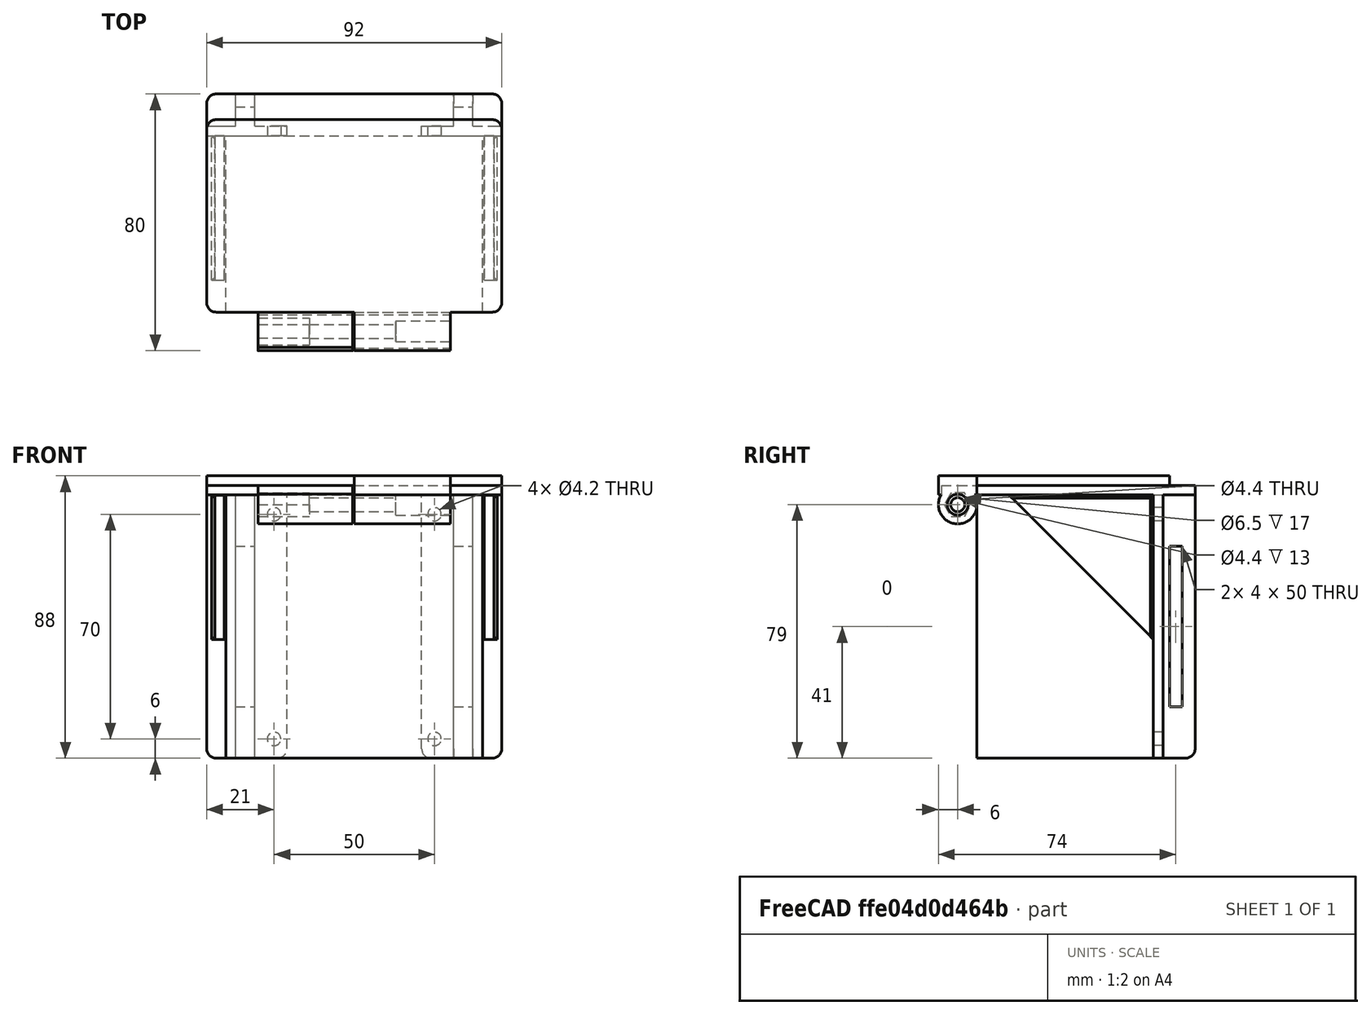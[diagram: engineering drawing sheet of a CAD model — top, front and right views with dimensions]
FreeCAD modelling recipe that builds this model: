
FCSTD DOCUMENT  (FreeCAD 0.15R4671 (Git))
Label: Enclosure_supports_with_Hood04
License: All rights reserved
LicenseURL: http://en.wikipedia.org/wiki/All_rights_reserved
objects: Drawing::FeatureViewPython×22, Part::Box×19, Part::Cut×10, Part::Cylinder×9, Part::MultiFuse×8, Part::Chamfer×8, Drawing::FeatureViewPart×2, Part::Fillet×2, Part::Prism×1, Drawing::FeaturePage×1
note: 57 computed .brp shape members not serialized (recipe doc carries the construction recipe); baked Part::Feature solids carry a one-line shape summary decoded from their .brp

FEATURE [Part::Box] Box  label="Cube"
  Height = 3
  Length = 92
  Placement = pos=(-6,0,0) rot=(0,0,1;0rad)
  Width = 68
FEATURE [Part::Cylinder] Cylinder
  Angle = 360
  Height = 29.5
  Placement = pos=(10,-6,-3) rot=(0,1,0;1.5708rad)
  Radius = 6
FEATURE [Part::Cylinder] Cylinder001
  Angle = 360
  Height = 30
  Placement = pos=(40,-6,-3) rot=(0,1,0;1.5708rad)
  Radius = 6
FEATURE [Part::Box] Box001  label="Cube001"
  Height = 3
  Length = 29.5
  Placement = pos=(10,-11,0) rot=(0,0,1;0rad)
  Width = 11
FEATURE [Part::Cylinder] Cylinder002
  Angle = 360
  Height = 30
  Placement = pos=(40,-6,-3) rot=(0,1,0;1.5708rad)
  Radius = 2.2
FEATURE [Part::Cylinder] Cylinder003
  Angle = 360
  Height = 30
  Placement = pos=(10,-6,-3) rot=(0,1,0;1.5708rad)
  Radius = 2.2
FEATURE [Part::Box] Box002  label="Cube002"
  Height = 3
  Length = 92
  Placement = pos=(-6,0,3) rot=(0,0,1;0rad)
  Width = 60
FEATURE [Part::Box] Box003  label="Cube003"
  Height = 6
  Length = 30
  Placement = pos=(40,-12,0) rot=(0,0,1;0rad)
  Width = 12
FEATURE [Part::Prism] Prism001
  Circumradius = 4.2
  Height = 16
  Placement = pos=(10,-6,-3) rot=(0.57735,0.57735,0.57735;2.0944rad)
  Polygon = 6
FEATURE [Part::Cylinder] Cylinder004
  Angle = 360
  Height = 17.5
  Placement = pos=(53,-6,-3) rot=(0,1,0;1.5708rad)
  Radius = 3.25
FEATURE [Part::Box] Box004  label="Cube004"
  Height = 45
  Length = 3
  Placement = pos=(80.5,10,-45) rot=(0,0,1;0rad)
  Width = 45
FEATURE [Part::Box] Box005  label="Cube005"
  Height = 45
  Length = 3
  Placement = pos=(-3.5,10,-45) rot=(0,0,1;0rad)
  Width = 45
FEATURE [Part::Box] Box006  label="Cube006"
  Height = 63.63
  Length = 3
  Placement = pos=(80.5,10,-90) rot=(1,0,0;0.785398rad)
  Width = 63.63
FEATURE [Part::Cut] Cut002
  Base = -> Box004
  Tool = -> Box006
FEATURE [Part::Box] Box007  label="Cube007"
  Height = 63.63
  Length = 3
  Placement = pos=(-3.5,10,-90) rot=(1,0,0;0.785398rad)
  Width = 63.63
FEATURE [Part::Cut] Cut003
  Base = -> Box005
  Tool = -> Box007
FEATURE [Part::Box] Box008  label="Cube008"
  Height = 82
  Length = 25
  Placement = pos=(-6,55,-82) rot=(0,0,1;0rad)
  Width = 3
FEATURE [Part::Box] Box009  label="Cube009"
  Height = 82
  Length = 25
  Placement = pos=(61,55,-82) rot=(0,0,1;0rad)
  Width = 3
FEATURE [Part::Cylinder] Cylinder005
  Angle = 360
  Height = 3
  Placement = pos=(15,58,-6) rot=(1,0,0;1.5708rad)
  Radius = 2.1
FEATURE [Part::Cylinder] Cylinder006
  Angle = 360
  Height = 3
  Placement = pos=(15,58,-76) rot=(1,0,0;1.5708rad)
  Radius = 2.1
FEATURE [Part::Cylinder] Cylinder007
  Angle = 360
  Height = 3
  Placement = pos=(65,58,-6) rot=(1,0,0;1.5708rad)
  Radius = 2.1
FEATURE [Part::Cylinder] Cylinder008
  Angle = 360
  Height = 3
  Placement = pos=(65,58,-76) rot=(1,0,0;1.5708rad)
  Radius = 2.1
FEATURE [Part::Box] Box011  label="Cube011"
  Height = 82
  Length = 6
  Placement = pos=(3,58,-82) rot=(0,0,1;0rad)
  Width = 10
FEATURE [Part::Box] Box012  label="Cube012"
  Height = 82
  Length = 6
  Placement = pos=(71,58,-82) rot=(0,0,1;0rad)
  Width = 10
FEATURE [Part::Box] Box013  label="Cube013"
  Height = 50
  Length = 6
  Placement = pos=(3,60,-66) rot=(0,0,1;0rad)
  Width = 4
FEATURE [Part::Box] Box014  label="Cube014"
  Height = 50
  Length = 6
  Placement = pos=(71,60,-66) rot=(0,0,1;0rad)
  Width = 4
FEATURE [Part::Box] Box015  label="G366"
  Height = 82
  Length = 80
  Placement = pos=(0,0,-82) rot=(0,0,1;0rad)
  Width = 55
FEATURE [Part::Cut] Cut
  Base = -> Cylinder
  Tool = -> Cylinder003
FEATURE [Part::Cut] Cut004
  Base = -> Cylinder001
  Tool = -> Cylinder002
FEATURE [Part::MultiFuse] Fusion
  Shapes = -> [Box,Box001,Cut]
FEATURE [Part::MultiFuse] Fusion001
  Shapes = -> [Cut004,Box003,Box002]
FEATURE [Part::Cut] Cut005
  Base = -> Fusion
  Tool = -> Prism001
FEATURE [Part::Cut] Cut006
  Base = -> Fusion001
  Tool = -> Cylinder004
FEATURE [Part::MultiFuse] Fusion002
  Shapes = -> [Cylinder005,Cylinder006]
FEATURE [Part::MultiFuse] Fusion003
  Shapes = -> [Cylinder007,Cylinder008]
FEATURE [Part::Cut] Cut007
  Base = -> Box008
  Tool = -> Fusion002
FEATURE [Part::Cut] Cut008
  Base = -> Box009
  Tool = -> Fusion003
FEATURE [Part::Cut] Cut009
  Base = -> Box011
  Tool = -> Box013
FEATURE [Part::Cut] Cut010
  Base = -> Box012
  Tool = -> Box014
FEATURE [Part::MultiFuse] Fusion004
  Shapes = -> [Cut007,Cut009]
FEATURE [Part::MultiFuse] Fusion005
  Shapes = -> [Cut008,Cut010]
FEATURE [Part::MultiFuse] Fusion006
  Shapes = -> [Cut002,Cut003,Cut005,Fusion004,Fusion005]
FEATURE [Drawing::FeatureViewPart] Ortho001  label="Ortho_-1_0"
  Direction = (0,1,0)
  HiddenWidth = 0.15
  LineWidth = 0.35
  Rotation = -90
  ShowHiddenLines = false
  ShowSmoothLines = false
  Source = -> Fusion006
  Tolerance = 0.05
  ViewResult = <g id="Ortho_-1_0"\n   transform="rotate(-90,125.25,42) translate(125.25,42) scale(1,1)"\n  >\n<g   stroke="rgb(0, 0, 0)"\n   stroke-width="0.35"\n   stroke-linecap="butt"\n   stroke-linejoin="miter"\n   fill="none"\n   transform="scale(1,-1)"\n  >\n<path id= "1" d=" M 0 9 L 0 71 " />\n<path id= "2" d=" M 0 -6 L 3 -6 " />\n<path id= "3" d=" M -82 19 L 0 19 " />\n<path id= "4" d=" M -82 9 L -82 19 " />\n<circle cx ="-76" cy ="15" r ="2.1" /><circle cx ="-6" cy ="15" r ="2.1" /><path id= "7" d=" M -82 9 L 0 9 " />\n<path id= "8" d=" M 0 -6 L 0 3 " />\n<path id= "9" d=" M 0 3 L 0 9 " />\n<path id= "10" d=" M 3 -6 L 3 86 " />\n<path id= "11" d=" M 0 86 L 3 86 " />\n<path id= "12" d=" M 0 71 L 0 77 " />\n<path id= "13" d=" M 0 77 L 0 86 " />\n<path id= "14" d=" M -82 71 L 0 71 " />\n<path id= "15" d=" M -82 61 L -82 71 " />\n<path id= "16" d=" M -82 61 L 0 61 " />\n<circle cx ="-6" cy ="65" r ="2.1" /><circle cx ="-76" cy ="65" r ="2.1" /><path id= "19" d=" M -82 86 L 0 86 " />\n<path id= "20" d=" M -82 77 L -82 86 " />\n<path id= "21" d=" M -82 -6 L 0 -6 " />\n<path id= "22" d=" M -82 -6 L -82 3 " />\n<path id= "23" d=" M -82 3 L -82 9 " />\n<path id= "24" d=" M -82 3 L 0 3 " />\n<path id= "25" d=" M -82 71 L -82 77 " />\n<path id= "26" d=" M -82 77 L 0 77 " />\n<path d="M-9,39.5 L-8.93298,39.5  L-8.73344,39.5  L-8.40581,39.5  L-7.95743,39.5  L-7.39831,39.5  L-6.74094,39.5  L-6,39.5  L-5.19205,39.5  L-4.33513,39.5  L-3.44838,39.5  L-2.55162,39.5  L-1.66487,39.5  L-0.807954,39.5  L8.21565e-14,39.5 " /><path id= "28" d=" M -9 19 L -9 39.5 " />\n</g>\n</g>
  Visible = true
  X = 125.25
  Y = 42
FEATURE [Drawing::FeatureViewPart] Ortho002  label="Ortho_1_0"
  Direction = (0,-1,0)
  HiddenWidth = 0.15
  LineWidth = 0.35
  Rotation = 90
  ShowHiddenLines = false
  ShowSmoothLines = false
  Source = -> Fusion006
  Tolerance = 0.05
  ViewResult = <blob: 2087 chars omitted>
  Visible = true
  X = 174.75
  Y = 42
FEATURE [Drawing::FeatureViewPython] dim001  # drawing view (typed FeaturePython)
  Rotation = 0
  ViewResult = <g> \n  <line x1="166.750000" y1="124.000000" x2="154.257392" y2="124.000000" style="stroke:rgb(0,0,255);stroke-width:0.50" />\n<line x1="166.750000" y1="42.000000" x2="154.257392" y2="42.000000" style="stroke:rgb(0,0,255);stroke-width:0.50" />\n<line x1="155.257392" y1="124.000000" x2="155.257392" y2="42.000000" style="stroke:rgb(0,0,255);stroke-width:0.50" /> \n  <polygon points="155.257392,42.000000 154.257392,45.000000 155.257392,46.000000 156.257392,45.000000" style="fill:rgb(0,0,255);stroke:rgb(0,0,255);stroke-width:0" /><polygon points="155.257392,124.000000 156.257392,121.000000 155.257392,120.000000 154.257392,121.000000" style="fill:rgb(0,0,255);stroke:rgb(0,0,255);stroke-width:0" /> \n  <text x="153.257392" y="83.000000" font-family="inherit" font-size="3.6" fill="rgb(0,0,255)" text-anchor="middle" transform="rotate(-90.000000 153.257392,83.000000)" >82</text> </g>
  Visible = true
  X = 0
  Y = 0
  arrowL1 = 3
  arrowL2 = 1
  arrowW = 2
  arrow_scheme = 0
  autoPlaceOffset = 2
  autoPlaceText = true
  click1_x = 155.257
  click1_y = 108.709
  click2_x = 155.257
  click2_y = 108.709
  comma_decimal_place = false
  dimension_line_overshoot = 1
  gap_datum_points = 2
  halfDimension_linear = false
  lineColor = rgb(0,0,255)
  strokeWidth = 0.5
  textFormat_linear = %(value)3.3f
  textRenderer_color = rgb(0,0,255)
  textRenderer_family = inherit
  textRenderer_size = 3.6
  unit_custom_scale = 1
  unit_scheme = 0
FEATURE [Drawing::FeatureViewPython] dim002  # drawing view (typed FeaturePython)
  Rotation = 0
  ViewResult = <g> \n  <line x1="214.250000" y1="40.000000" x2="214.250000" y2="33.983509" style="stroke:rgb(0,0,255);stroke-width:0.50" />\n<line x1="260.750000" y1="40.000000" x2="260.750000" y2="33.983509" style="stroke:rgb(0,0,255);stroke-width:0.50" />\n<line x1="214.250000" y1="34.983509" x2="260.750000" y2="34.983509" style="stroke:rgb(0,0,255);stroke-width:0.50" /> \n  <polygon points="260.750000,34.983509 257.750000,33.983509 256.750000,34.983509 257.750000,35.983509" style="fill:rgb(0,0,255);stroke:rgb(0,0,255);stroke-width:0" /><polygon points="214.250000,34.983509 217.250000,35.983509 218.250000,34.983509 217.250000,33.983509" style="fill:rgb(0,0,255);stroke:rgb(0,0,255);stroke-width:0" /> \n  <text x="237.500000" y="32.983509" font-family="inherit" font-size="3.6" fill="rgb(0,0,255)" text-anchor="middle" transform="rotate(0.000000 237.500000,32.983509)" >46.5</text> </g>
  Visible = true
  X = 0
  Y = 0
  arrowL1 = 3
  arrowL2 = 1
  arrowW = 2
  arrow_scheme = 0
  autoPlaceOffset = 2
  autoPlaceText = true
  click1_x = 220.02
  click1_y = 34.9835
  click2_x = 220.02
  click2_y = 34.9835
  comma_decimal_place = false
  dimension_line_overshoot = 1
  gap_datum_points = 2
  halfDimension_linear = false
  lineColor = rgb(0,0,255)
  strokeWidth = 0.5
  textFormat_linear = %(value)3.3f
  textRenderer_color = rgb(0,0,255)
  textRenderer_family = inherit
  textRenderer_size = 3.6
  unit_custom_scale = 1
  unit_scheme = 0
FEATURE [Drawing::FeatureViewPython] centerLines001  # drawing view (typed FeaturePython)
  Rotation = 0
  ViewResult = <g transform="scale(1.000000,1.000000)" stroke="rgb(0,0,255)"  stroke-width="0.320000" > <path d="M 189.750000,118.000000 L 189.750000,121.000000 M 189.750000,123.000000 L 189.750000,124.803428 "/>\n<path d="M 189.750000,118.000000 L 192.750000,118.000000 M 194.750000,118.000000 L 197.083406,118.000000 "/>\n<path d="M 189.750000,118.000000 L 189.750000,115.000000 M 189.750000,113.000000 L 189.750000,108.179034 "/>\n<path d="M 189.750000,118.000000 L 186.750000,118.000000 M 184.750000,118.000000 L 182.145544,118.000000 "/> </g> 
  Visible = true
  X = 0
  Y = 0
  centerLine_color = rgb(0,0,255)
  centerLine_len_dash = 6
  centerLine_len_dot = 3
  centerLine_len_gap = 2
  centerLine_width = 0.32
  click1_x = 197.083
  click1_y = 124.803
  click2_x = 182.146
  click2_y = 108.179
FEATURE [Drawing::FeatureViewPython] centerLines002  # drawing view (typed FeaturePython)
  Rotation = 0
  ViewResult = <g transform="scale(1.000000,1.000000)" stroke="rgb(0,0,255)"  stroke-width="0.320000" > <path d="M 189.750000,118.000000 L 189.750000,121.000000 M 189.750000,123.000000 L 189.750000,126.008095 "/>\n<path d="M 189.750000,118.000000 L 192.750000,118.000000 M 194.750000,118.000000 L 200.750000,118.000000 M 202.750000,118.000000 L 205.750000,118.000000 M 207.750000,118.000000 L 213.750000,118.000000 M 215.750000,118.000000 L 218.750000,118.000000 M 220.750000,118.000000 L 226.750000,118.000000 M 228.750000,118.000000 L 231.750000,118.000000 M 233.750000,118.000000 L 239.750000,118.000000 M 241.750000,118.000000 L 244.750000,118.000000 M 246.750000,118.000000 L 249.847790,118.000000 "/>\n<path d="M 189.750000,118.000000 L 189.750000,115.000000 M 189.750000,113.000000 L 189.750000,107.697167 "/>\n<path d="M 189.750000,118.000000 L 192.750000,118.000000 M 194.750000,118.000000 L 200.750000,118.000000 M 202.750000,118.000000 L 205.750000,118.000000 M 207.750000,118.000000 L 213.750000,118.000000 M 215.750000,118.000000 L 218.750000,118.000000 M 220.750000,118.000000 L 223.826998,118.000000 "/> </g> 
  Visible = true
  X = 0
  Y = 0
  centerLine_color = rgb(0,0,255)
  centerLine_len_dash = 6
  centerLine_len_dot = 3
  centerLine_len_gap = 2
  centerLine_width = 0.32
  click1_x = 249.848
  click1_y = 126.008
  click2_x = 223.827
  click2_y = 107.697
FEATURE [Drawing::FeatureViewPython] centerLines003  # drawing view (typed FeaturePython)
  Rotation = 0
  ViewResult = <g transform="scale(1.000000,1.000000)" stroke="rgb(0,0,255)"  stroke-width="0.320000" > <path d="M 189.750000,118.000000 L 189.750000,115.000000 M 189.750000,113.000000 L 189.750000,107.000000 M 189.750000,105.000000 L 189.750000,102.000000 M 189.750000,100.000000 L 189.750000,94.000000 M 189.750000,92.000000 L 189.750000,89.000000 M 189.750000,87.000000 L 189.750000,81.000000 M 189.750000,79.000000 L 189.750000,76.000000 M 189.750000,74.000000 L 189.750000,68.000000 M 189.750000,66.000000 L 189.750000,63.000000 M 189.750000,61.000000 L 189.750000,56.378383 "/>\n<path d="M 189.750000,118.000000 L 192.750000,118.000000 M 194.750000,118.000000 L 200.750000,118.000000 M 202.750000,118.000000 L 205.750000,118.000000 M 207.750000,118.000000 L 213.750000,118.000000 M 215.750000,118.000000 L 218.750000,118.000000 M 220.750000,118.000000 L 226.750000,118.000000 M 228.750000,118.000000 L 231.750000,118.000000 M 233.750000,118.000000 L 239.750000,118.000000 M 241.750000,118.000000 L 244.750000,118.000000 "/>\n<path d="M 189.750000,118.000000 L 189.750000,115.000000 M 189.750000,113.000000 L 189.750000,107.000000 M 189.750000,105.000000 L 189.750000,102.000000 M 189.750000,100.000000 L 189.750000,94.000000 M 189.750000,92.000000 L 189.750000,89.000000 M 189.750000,87.000000 L 189.750000,81.000000 M 189.750000,79.000000 L 189.750000,76.000000 M 189.750000,74.000000 L 189.750000,68.000000 M 189.750000,66.000000 L 189.750000,63.000000 M 189.750000,61.000000 L 189.750000,55.000000 M 189.750000,53.000000 L 189.750000,50.000000 M 189.750000,48.000000 L 189.750000,42.163320 "/>\n<path d="M 189.750000,118.000000 L 192.750000,118.000000 M 194.750000,118.000000 L 200.750000,118.000000 M 202.750000,118.000000 L 205.750000,118.000000 M 207.750000,118.000000 L 213.750000,118.000000 M 215.750000,118.000000 L 218.750000,118.000000 M 220.750000,118.000000 L 226.750000,118.000000 "/> </g> 
  Visible = true
  X = 0
  Y = 0
  centerLine_color = rgb(0,0,255)
  centerLine_len_dash = 6
  centerLine_len_dot = 3
  centerLine_len_gap = 2
  centerLine_width = 0.32
  click1_x = 246.475
  click1_y = 56.3784
  click2_x = 227.923
  click2_y = 42.1633
FEATURE [Drawing::FeatureViewPython] dim003  # drawing view (typed FeaturePython)
  Rotation = 0
  ViewResult = <g> \n  <line x1="189.750000" y1="116.000000" x2="189.750000" y2="111.770659" style="stroke:rgb(0,0,255);stroke-width:0.50" />\n<line x1="197.083406" y1="116.000000" x2="197.083406" y2="111.770659" style="stroke:rgb(0,0,255);stroke-width:0.50" />\n<line x1="189.750000" y1="112.770659" x2="197.083406" y2="112.770659" style="stroke:rgb(0,0,255);stroke-width:0.50" /> \n  <polygon points="197.083406,112.770659 200.083406,113.770659 201.083406,112.770659 200.083406,111.770659" style="fill:rgb(0,0,255);stroke:rgb(0,0,255);stroke-width:0" /><polygon points="189.750000,112.770659 186.750000,111.770659 185.750000,112.770659 186.750000,113.770659" style="fill:rgb(0,0,255);stroke:rgb(0,0,255);stroke-width:0" /> \n  <text x="193.416703" y="110.770659" font-family="inherit" font-size="3.6" fill="rgb(0,0,255)" text-anchor="middle" transform="rotate(0.000000 193.416703,110.770659)" >7.333</text> </g>
  Visible = true
  X = 0
  Y = 0
  arrowL1 = 3
  arrowL2 = 1
  arrowW = 2
  arrow_scheme = 0
  autoPlaceOffset = 2
  autoPlaceText = true
  click1_x = 200.722
  click1_y = 112.771
  click2_x = 200.722
  click2_y = 112.771
  comma_decimal_place = false
  dimension_line_overshoot = 1
  gap_datum_points = 2
  halfDimension_linear = false
  lineColor = rgb(0,0,255)
  strokeWidth = 0.5
  textFormat_linear = %(value)3.3f
  textRenderer_color = rgb(0,0,255)
  textRenderer_family = inherit
  textRenderer_size = 3.6
  unit_custom_scale = 1
  unit_scheme = 0
FEATURE [Drawing::FeatureViewPython] centerLines004  # drawing view (typed FeaturePython)
  Rotation = 0
  ViewResult = <g transform="scale(1.000000,1.000000)" stroke="rgb(0,0,255)"  stroke-width="0.320000" > <path d="M 110.250000,48.000000 L 110.250000,51.000000 M 110.250000,53.000000 L 110.250000,59.000000 "/>\n<path d="M 110.250000,48.000000 L 110.250000,45.000000 M 110.250000,43.000000 L 110.250000,37.000000 M 110.250000,35.000000 L 110.250000,34.274134 "/> </g> 
  Visible = true
  X = 0
  Y = 0
  centerLine_color = rgb(0,0,255)
  centerLine_len_dash = 6
  centerLine_len_dot = 3
  centerLine_len_gap = 2
  centerLine_width = 0.32
  click1_x = 114.186
  click1_y = 60.4838
  click2_x = 114.003
  click2_y = 34.2741
FEATURE [Drawing::FeatureViewPython] dimStack001  # drawing view (typed FeaturePython)
  Rotation = 0
  ViewResult = <g> <line x1="189.750000" y1="106.179033" x2="189.750000" y2="80.378158" style="stroke:rgb(0,0,255);stroke-width:0.50" />\n<line x1="226.750000" y1="115.999999" x2="226.750000" y2="80.378158" style="stroke:rgb(0,0,255);stroke-width:0.50" />\n<line x1="189.750000" y1="81.378158" x2="226.750000" y2="81.378158" style="stroke:rgb(0,0,255);stroke-width:0.50" />\n<polygon points="189.750000,81.378158 192.750000,82.378158 193.750000,81.378158 192.750000,80.378158" style="fill:rgb(0,0,255);stroke:rgb(0,0,255);stroke-width:0" />\n<polygon points="226.750000,81.378158 223.750000,80.378158 222.750000,81.378158 223.750000,82.378158" style="fill:rgb(0,0,255);stroke:rgb(0,0,255);stroke-width:0" />\n<text x="208.250000" y="79.378158" font-family="inherit" font-size="3.6" fill="rgb(0,0,255)" text-anchor="middle" transform="rotate(0.000000 208.250000,79.378158)" >37</text> </g> 
  Visible = true
  X = 0
  Y = 0
  arrowL1 = 3
  arrowL2 = 1
  arrowW = 2
  arrow_scheme = 0
  autoPlaceOffset = 2
  click1_x = 210.777
  click1_y = 81.3782
  comma_decimal_place = false
  dimension_line_overshoot = 1
  gap_datum_points = 2
  lineColor = rgb(0,0,255)
  stack_offset = 7
  stack_offset0 = 0
  strokeWidth = 0.5
  textFormat_linear = %(value)3.3f
  textRenderer_color = rgb(0,0,255)
  textRenderer_family = inherit
  textRenderer_size = 3.6
  unit_custom_scale = 1
  unit_scheme = 0
FEATURE [Drawing::FeatureViewPython] dimStack002  # drawing view (typed FeaturePython)
  Rotation = 0
  ViewResult = <g> <line x1="168.750000" y1="126.000000" x2="168.750000" y2="129.298898" style="stroke:rgb(0,0,255);stroke-width:0.50" />\n<line x1="260.750000" y1="126.000000" x2="260.750000" y2="129.298898" style="stroke:rgb(0,0,255);stroke-width:0.50" />\n<line x1="168.750000" y1="128.298898" x2="260.750000" y2="128.298898" style="stroke:rgb(0,0,255);stroke-width:0.50" />\n<polygon points="168.750000,128.298898 171.750000,129.298898 172.750000,128.298898 171.750000,127.298898" style="fill:rgb(0,0,255);stroke:rgb(0,0,255);stroke-width:0" />\n<polygon points="260.750000,128.298898 257.750000,127.298898 256.750000,128.298898 257.750000,129.298898" style="fill:rgb(0,0,255);stroke:rgb(0,0,255);stroke-width:0" />\n<text x="214.750000" y="126.298898" font-family="inherit" font-size="3.6" fill="rgb(0,0,255)" text-anchor="middle" transform="rotate(0.000000 214.750000,126.298898)" >92</text> </g> 
  Visible = true
  X = 0
  Y = 0
  arrowL1 = 3
  arrowL2 = 1
  arrowW = 2
  arrow_scheme = 0
  autoPlaceOffset = 2
  click1_x = 214.076
  click1_y = 128.299
  comma_decimal_place = false
  dimension_line_overshoot = 1
  gap_datum_points = 2
  lineColor = rgb(0,0,255)
  stack_offset = 7
  stack_offset0 = 0
  strokeWidth = 0.5
  textFormat_linear = %(value)3.3f
  textRenderer_color = rgb(0,0,255)
  textRenderer_family = inherit
  textRenderer_size = 3.6
  unit_custom_scale = 1
  unit_scheme = 0
FEATURE [Drawing::FeatureViewPython] dimStack003  # drawing view (typed FeaturePython)
  Rotation = 0
  ViewResult = <g> <line x1="193.750000" y1="98.240299" x2="235.750000" y2="98.240299" style="stroke:rgb(0,0,255);stroke-width:0.50" />\n<polygon points="193.750000,98.240299 196.750000,99.240299 197.750000,98.240299 196.750000,97.240299" style="fill:rgb(0,0,255);stroke:rgb(0,0,255);stroke-width:0" />\n<polygon points="235.750000,98.240299 232.750000,97.240299 231.750000,98.240299 232.750000,99.240299" style="fill:rgb(0,0,255);stroke:rgb(0,0,255);stroke-width:0" />\n<text x="214.750000" y="96.240299" font-family="inherit" font-size="3.6" fill="rgb(0,0,255)" text-anchor="middle" transform="rotate(0.000000 214.750000,96.240299)" >42</text> </g> 
  Visible = true
  X = 0
  Y = 0
  arrowL1 = 3
  arrowL2 = 1
  arrowW = 2
  arrow_scheme = 0
  autoPlaceOffset = 2
  click1_x = 217.008
  click1_y = 98.2403
  comma_decimal_place = false
  dimension_line_overshoot = 1
  gap_datum_points = 2
  lineColor = rgb(0,0,255)
  stack_offset = 7
  stack_offset0 = 0
  strokeWidth = 0.5
  textFormat_linear = %(value)3.3f
  textRenderer_color = rgb(0,0,255)
  textRenderer_family = inherit
  textRenderer_size = 3.6
  unit_custom_scale = 1
  unit_scheme = 0
FEATURE [Drawing::FeatureViewPython] centerLines005  # drawing view (typed FeaturePython)
  Rotation = 0
  ViewResult = <g transform="scale(1.000000,1.000000)" stroke="rgb(0,0,255)"  stroke-width="0.320000" > <path d="M 60.250000,118.000000 L 60.250000,115.000000 M 60.250000,113.000000 L 60.250000,107.000000 M 60.250000,105.000000 L 60.250000,104.591016 "/>\n<path d="M 60.250000,118.000000 L 60.250000,121.000000 M 60.250000,123.000000 L 60.250000,129.000000 M 60.250000,131.000000 L 60.250000,133.968174 "/> </g> 
  Visible = true
  X = 0
  Y = 0
  centerLine_color = rgb(0,0,255)
  centerLine_len_dash = 6
  centerLine_len_dot = 3
  centerLine_len_gap = 2
  centerLine_width = 0.32
  click1_x = 60.4211
  click1_y = 104.591
  click2_x = 59.7961
  click2_y = 133.968
FEATURE [Drawing::FeatureViewPython] centerLines006  # drawing view (typed FeaturePython)
  Rotation = 0
  ViewResult = <g transform="scale(1.000000,1.000000)" stroke="rgb(0,0,255)"  stroke-width="0.320000" > <path d="M 110.250000,118.000000 L 110.250000,115.000000 M 110.250000,113.000000 L 110.250000,107.000000 "/>\n<path d="M 110.250000,118.000000 L 110.250000,121.000000 M 110.250000,123.000000 L 110.250000,129.000000 M 110.250000,131.000000 L 110.250000,132.926431 "/> </g> 
  Visible = true
  X = 0
  Y = 0
  centerLine_color = rgb(0,0,255)
  centerLine_len_dash = 6
  centerLine_len_dot = 3
  centerLine_len_gap = 2
  centerLine_width = 0.32
  click1_x = 109.175
  click1_y = 105.841
  click2_x = 110.216
  click2_y = 132.926
FEATURE [Drawing::FeatureViewPython] dim004  # drawing view (typed FeaturePython)
  Rotation = 0
  ViewResult = <g> \n  <line x1="60.250000" y1="135.968174" x2="60.250000" y2="140.385239" style="stroke:rgb(0,0,255);stroke-width:0.50" />\n<line x1="110.250000" y1="134.926431" x2="110.250000" y2="140.385239" style="stroke:rgb(0,0,255);stroke-width:0.50" />\n<line x1="60.250000" y1="139.385239" x2="110.250000" y2="139.385239" style="stroke:rgb(0,0,255);stroke-width:0.50" /> \n  <polygon points="110.250000,139.385239 107.250000,138.385239 106.250000,139.385239 107.250000,140.385239" style="fill:rgb(0,0,255);stroke:rgb(0,0,255);stroke-width:0" /><polygon points="60.250000,139.385239 63.250000,140.385239 64.250000,139.385239 63.250000,138.385239" style="fill:rgb(0,0,255);stroke:rgb(0,0,255);stroke-width:0" /> \n  <text x="85.250000" y="137.385239" font-family="inherit" font-size="3.6" fill="rgb(0,0,255)" text-anchor="middle" transform="rotate(0.000000 85.250000,137.385239)" >50</text> </g>
  Visible = true
  X = 0
  Y = 0
  arrowL1 = 3
  arrowL2 = 1
  arrowW = 2
  arrow_scheme = 0
  autoPlaceOffset = 2
  autoPlaceText = true
  click1_x = 87.9231
  click1_y = 139.385
  click2_x = 87.9231
  click2_y = 139.385
  comma_decimal_place = false
  dimension_line_overshoot = 1
  gap_datum_points = 2
  halfDimension_linear = false
  lineColor = rgb(0,0,255)
  strokeWidth = 0.5
  textFormat_linear = %(value)3.3f
  textRenderer_color = rgb(0,0,255)
  textRenderer_family = inherit
  textRenderer_size = 3.6
  unit_custom_scale = 1
  unit_scheme = 0
FEATURE [Drawing::FeatureViewPython] centerLines007  # drawing view (typed FeaturePython)
  Rotation = 0
  ViewResult = <g transform="scale(1.000000,1.000000)" stroke="rgb(0,0,255)"  stroke-width="0.320000" > <path d="M 60.250000,48.000000 L 57.250000,48.000000 M 55.250000,48.000000 L 50.003673,48.000000 "/>\n<path d="M 60.250000,48.000000 L 63.250000,48.000000 M 65.250000,48.000000 L 71.250000,48.000000 "/> </g> 
  Visible = true
  X = 0
  Y = 0
  centerLine_color = rgb(0,0,255)
  centerLine_len_dash = 6
  centerLine_len_dot = 3
  centerLine_len_gap = 2
  centerLine_width = 0.32
  click1_x = 50.0037
  click1_y = 48.1285
  click2_x = 72.922
  click2_y = 45.8367
FEATURE [Drawing::FeatureViewPython] centerLines008  # drawing view (typed FeaturePython)
  Rotation = 0
  ViewResult = <g transform="scale(1.000000,1.000000)" stroke="rgb(0,0,255)"  stroke-width="0.320000" > <path d="M 60.250000,118.000000 L 57.250000,118.000000 M 55.250000,118.000000 L 49.250000,118.000000 M 47.250000,118.000000 L 46.878444,118.000000 "/>\n<path d="M 60.250000,118.000000 L 63.250000,118.000000 M 65.250000,118.000000 L 71.250000,118.000000 M 73.250000,118.000000 L 74.380464,118.000000 "/> </g> 
  Visible = true
  X = 0
  Y = 0
  centerLine_color = rgb(0,0,255)
  centerLine_len_dash = 6
  centerLine_len_dot = 3
  centerLine_len_gap = 2
  centerLine_width = 0.32
  click1_x = 46.8784
  click1_y = 119.175
  click2_x = 74.3805
  click2_y = 117.509
FEATURE [Drawing::FeatureViewPython] dim005  # drawing view (typed FeaturePython)
  Rotation = 0
  ViewResult = <g> \n  <line x1="58.250000" y1="48.000000" x2="34.835966" y2="48.000000" style="stroke:rgb(0,0,255);stroke-width:0.50" />\n<line x1="58.250000" y1="118.000000" x2="34.835966" y2="118.000000" style="stroke:rgb(0,0,255);stroke-width:0.50" />\n<line x1="35.835966" y1="48.000000" x2="35.835966" y2="118.000000" style="stroke:rgb(0,0,255);stroke-width:0.50" /> \n  <polygon points="35.835966,118.000000 36.835966,115.000000 35.835966,114.000000 34.835966,115.000000" style="fill:rgb(0,0,255);stroke:rgb(0,0,255);stroke-width:0" /><polygon points="35.835966,48.000000 34.835966,51.000000 35.835966,52.000000 36.835966,51.000000" style="fill:rgb(0,0,255);stroke:rgb(0,0,255);stroke-width:0" /> \n  <text x="33.835966" y="83.000000" font-family="inherit" font-size="3.6" fill="rgb(0,0,255)" text-anchor="middle" transform="rotate(-90.000000 33.835966,83.000000)" >70</text> </g>
  Visible = true
  X = 0
  Y = 0
  arrowL1 = 3
  arrowL2 = 1
  arrowW = 2
  arrow_scheme = 0
  autoPlaceOffset = 2
  autoPlaceText = true
  click1_x = 35.836
  click1_y = 112.717
  click2_x = 35.836
  click2_y = 112.717
  comma_decimal_place = false
  dimension_line_overshoot = 1
  gap_datum_points = 2
  halfDimension_linear = false
  lineColor = rgb(0,0,255)
  strokeWidth = 0.5
  textFormat_linear = %(value)3.3f
  textRenderer_color = rgb(0,0,255)
  textRenderer_family = inherit
  textRenderer_size = 3.6
  unit_custom_scale = 1
  unit_scheme = 0
FEATURE [Drawing::FeatureViewPython] dim006  # drawing view (typed FeaturePython)
  Rotation = 0
  ViewResult = <g> <line x1="54.250000" y1="85.839639" x2="116.250000" y2="85.839639" style="stroke:rgb(0,0,255);stroke-width:0.50" />\n<polygon points="54.250000,85.839639 57.250000,86.839639 58.250000,85.839639 57.250000,84.839639" style="fill:rgb(0,0,255);stroke:rgb(0,0,255);stroke-width:0" />\n<polygon points="116.250000,85.839639 113.250000,84.839639 112.250000,85.839639 113.250000,86.839639" style="fill:rgb(0,0,255);stroke:rgb(0,0,255);stroke-width:0" />\n<text x="85.250000" y="83.839639" font-family="inherit" font-size="3.6" fill="rgb(0,0,255)" text-anchor="middle" transform="rotate(0.000000 85.250000,83.839639)" >62</text> </g> 
  Visible = true
  X = 0
  Y = 0
  arrowL1 = 3
  arrowL2 = 1
  arrowW = 2
  arrow_scheme = 0
  autoPlaceOffset = 2
  autoPlaceText = true
  click1_x = 88.1315
  click1_y = 85.8396
  click2_x = 88.1315
  click2_y = 85.8396
  comma_decimal_place = false
  dimension_line_overshoot = 1
  gap_datum_points = 2
  halfDimension_linear = false
  lineColor = rgb(0,0,255)
  strokeWidth = 0.5
  textFormat_linear = %(value)3.3f
  textRenderer_color = rgb(0,0,255)
  textRenderer_family = inherit
  textRenderer_size = 3.6
  unit_custom_scale = 1
  unit_scheme = 0
FEATURE [Drawing::FeatureViewPython] dim007  # drawing view (typed FeaturePython)
  Rotation = 0
  ViewResult = <g> \n  <line x1="50.250000" y1="124.000000" x2="124.134045" y2="124.000000" style="stroke:rgb(0,0,255);stroke-width:0.50" />\n<line x1="50.250000" y1="42.000000" x2="124.134045" y2="42.000000" style="stroke:rgb(0,0,255);stroke-width:0.50" />\n<line x1="123.134045" y1="124.000000" x2="123.134045" y2="42.000000" style="stroke:rgb(0,0,255);stroke-width:0.50" /> \n  <polygon points="123.134045,42.000000 122.134045,45.000000 123.134045,46.000000 124.134045,45.000000" style="fill:rgb(0,0,255);stroke:rgb(0,0,255);stroke-width:0" /><polygon points="123.134045,124.000000 124.134045,121.000000 123.134045,120.000000 122.134045,121.000000" style="fill:rgb(0,0,255);stroke:rgb(0,0,255);stroke-width:0" /> \n  <text x="121.134045" y="83.000000" font-family="inherit" font-size="3.6" fill="rgb(0,0,255)" text-anchor="middle" transform="rotate(-90.000000 121.134045,83.000000)" >82</text> </g>
  Visible = true
  X = 0
  Y = 0
  arrowL1 = 3
  arrowL2 = 1
  arrowW = 2
  arrow_scheme = 0
  autoPlaceOffset = 2
  autoPlaceText = true
  click1_x = 123.134
  click1_y = 93.1318
  click2_x = 123.134
  click2_y = 93.1318
  comma_decimal_place = false
  dimension_line_overshoot = 1
  gap_datum_points = 2
  halfDimension_linear = false
  lineColor = rgb(0,0,255)
  strokeWidth = 0.5
  textFormat_linear = %(value)3.3f
  textRenderer_color = rgb(0,0,255)
  textRenderer_family = inherit
  textRenderer_size = 3.6
  unit_custom_scale = 1
  unit_scheme = 0
FEATURE [Drawing::FeatureViewPython] dim008  # drawing view (typed FeaturePython)
  Rotation = 0
  ViewResult = <g> <line x1="122.250000" y1="73.755418" x2="48.250000" y2="73.755418" style="stroke:rgb(0,0,255);stroke-width:0.50" />\n<polygon points="122.250000,73.755418 119.250000,72.755418 118.250000,73.755418 119.250000,74.755418" style="fill:rgb(0,0,255);stroke:rgb(0,0,255);stroke-width:0" />\n<polygon points="48.250000,73.755418 51.250000,74.755418 52.250000,73.755418 51.250000,72.755418" style="fill:rgb(0,0,255);stroke:rgb(0,0,255);stroke-width:0" />\n<text x="85.250000" y="71.755418" font-family="inherit" font-size="3.6" fill="rgb(0,0,255)" text-anchor="middle" transform="rotate(0.000000 85.250000,71.755418)" >74</text> </g> 
  Visible = true
  X = 0
  Y = 0
  arrowL1 = 3
  arrowL2 = 1
  arrowW = 2
  arrow_scheme = 0
  autoPlaceOffset = 2
  autoPlaceText = true
  click1_x = 71.0469
  click1_y = 73.7554
  click2_x = 71.0469
  click2_y = 73.7554
  comma_decimal_place = false
  dimension_line_overshoot = 1
  gap_datum_points = 2
  halfDimension_linear = false
  lineColor = rgb(0,0,255)
  strokeWidth = 0.5
  textFormat_linear = %(value)3.3f
  textRenderer_color = rgb(0,0,255)
  textRenderer_family = inherit
  textRenderer_size = 3.6
  unit_custom_scale = 1
  unit_scheme = 0
FEATURE [Drawing::FeatureViewPython] dim009  # drawing view (typed FeaturePython)
  Rotation = 0
  ViewResult = <g> <line x1="39.250000" y1="66.046518" x2="131.250000" y2="66.046518" style="stroke:rgb(0,0,255);stroke-width:0.50" />\n<polygon points="39.250000,66.046518 42.250000,67.046518 43.250000,66.046518 42.250000,65.046518" style="fill:rgb(0,0,255);stroke:rgb(0,0,255);stroke-width:0" />\n<polygon points="131.250000,66.046518 128.250000,65.046518 127.250000,66.046518 128.250000,67.046518" style="fill:rgb(0,0,255);stroke:rgb(0,0,255);stroke-width:0" />\n<text x="85.250000" y="64.046518" font-family="inherit" font-size="3.6" fill="rgb(0,0,255)" text-anchor="middle" transform="rotate(0.000000 85.250000,64.046518)" >92</text> </g> 
  Visible = true
  X = 0
  Y = 0
  arrowL1 = 3
  arrowL2 = 1
  arrowW = 2
  arrow_scheme = 0
  autoPlaceOffset = 2
  autoPlaceText = true
  click1_x = 114.8
  click1_y = 66.0465
  click2_x = 114.8
  click2_y = 66.0465
  comma_decimal_place = false
  dimension_line_overshoot = 1
  gap_datum_points = 2
  halfDimension_linear = false
  lineColor = rgb(0,0,255)
  strokeWidth = 0.5
  textFormat_linear = %(value)3.3f
  textRenderer_color = rgb(0,0,255)
  textRenderer_family = inherit
  textRenderer_size = 3.6
  unit_custom_scale = 1
  unit_scheme = 0
FEATURE [Drawing::FeatureViewPython] dim010  # drawing view (typed FeaturePython)
  Rotation = 0
  ViewResult = <g> <line x1="174.250000" y1="64.004702" x2="255.250000" y2="64.004702" style="stroke:rgb(0,0,255);stroke-width:0.50" />\n<polygon points="174.250000,64.004702 177.250000,65.004702 178.250000,64.004702 177.250000,63.004702" style="fill:rgb(0,0,255);stroke:rgb(0,0,255);stroke-width:0" />\n<polygon points="255.250000,64.004702 252.250000,63.004702 251.250000,64.004702 252.250000,65.004702" style="fill:rgb(0,0,255);stroke:rgb(0,0,255);stroke-width:0" />\n<text x="214.750000" y="62.004702" font-family="inherit" font-size="3.6" fill="rgb(0,0,255)" text-anchor="middle" transform="rotate(0.000000 214.750000,62.004702)" >81</text> </g> 
  Visible = true
  X = 0
  Y = 0
  arrowL1 = 3
  arrowL2 = 1
  arrowW = 2
  arrow_scheme = 0
  autoPlaceOffset = 2
  autoPlaceText = true
  click1_x = 227.267
  click1_y = 64.0047
  click2_x = 227.267
  click2_y = 64.0047
  comma_decimal_place = false
  dimension_line_overshoot = 1
  gap_datum_points = 2
  halfDimension_linear = false
  lineColor = rgb(0,0,255)
  strokeWidth = 0.5
  textFormat_linear = %(value)3.3f
  textRenderer_color = rgb(0,0,255)
  textRenderer_family = inherit
  textRenderer_size = 3.6
  unit_custom_scale = 1
  unit_scheme = 0
FEATURE [Part::Box] Box016  label="Cube015"
  Height = 1
  Length = 1
  Placement = pos=(-4.5,10,-1) rot=(0,0,1;0rad)
  Width = 45
FEATURE [Part::Box] Box017  label="Cube016"
  Height = 45
  Length = 1
  Placement = pos=(-4.5,54,-45) rot=(0,0,1;0rad)
  Width = 1
FEATURE [Part::Box] Box018  label="Cube017"
  Height = 45
  Length = 1
  Placement = pos=(83.5,54,-45) rot=(0,0,1;0rad)
  Width = 1
FEATURE [Part::Box] Box019  label="Cube018"
  Height = 1
  Length = 1
  Placement = pos=(83.5,10,-1) rot=(0,0,1;0rad)
  Width = 45
FEATURE [Part::Chamfer] Chamfer
  Base = -> Box016
  Edges = 1 edges r=0.9: [Edge9]
FEATURE [Part::Chamfer] Chamfer001
  Base = -> Box017
  Edges = 1 edges r=0.9: [Edge9]
FEATURE [Part::Chamfer] Chamfer002
  Base = -> Box018
  Edges = 1 edges r=0.9: [Edge9]
FEATURE [Part::Chamfer] Chamfer003
  Base = -> Box019
  Edges = 1 edges r=0.9: [Edge9]
FEATURE [Part::Chamfer] Chamfer004
  Base = -> Chamfer003
  Edges = 1 edges r=0.99: [Edge14]
FEATURE [Part::Chamfer] Chamfer005
  Base = -> Chamfer002
  Edges = 1 edges r=0.99: [Edge6]
FEATURE [Part::Chamfer] Chamfer006
  Base = -> Chamfer001
  Edges = 1 edges r=0.99: [Edge1]
FEATURE [Part::Chamfer] Chamfer007
  Base = -> Chamfer
  Edges = 1 edges r=0.99: [Edge4]
FEATURE [Drawing::FeatureViewPython] dia  # drawing view (typed FeaturePython)
  Rotation = 0
  ViewResult = <g>  <circle cx ="60.250000" cy ="118.000000" r="0.250000" stroke="none" fill="rgb(0,0,255)" /> \n<line x1="67.324946" y1="129.249494" x2="59.132005" y2="116.222336" style="stroke:rgb(0,0,255);stroke-width:0.50" />\n<polygon points="61.367995,119.777664 62.118623,122.849562 63.497508,123.163690 63.811636,121.784805" style="fill:rgb(0,0,255);stroke:rgb(0,0,255);stroke-width:0" />\n<polygon points="59.132005,116.222336 58.381377,113.150438 57.002492,112.836310 56.688364,114.215195" style="fill:rgb(0,0,255);stroke:rgb(0,0,255);stroke-width:0" />\n<line x1="67.324946" y1="129.249494" x2="78.125739" y2="129.249494" style="stroke:rgb(0,0,255);stroke-width:0.50" />\n<text x="72.725342" y="127.249494" font-family="inherit" font-size="3.6" fill="rgb(0,0,255)" text-anchor="middle" transform="rotate(0.000000 72.725342,127.249494)" >Ø4.2</text> </g>
  Visible = true
  X = 0
  Y = 0
  arrowL1 = 3
  arrowL2 = 1
  arrowW = 2
  arrow_scheme = 0
  autoPlaceOffset = 2
  autoPlaceText = true
  centerPointDia = 0.5
  click1_x = 67.3249
  click1_y = 129.249
  click2_x = 78.1257
  click2_y = 130.33
  click3_x = 78.1257
  click3_y = 130.33
  comma_decimal_place = false
  lineColor = rgb(0,0,255)
  strokeWidth = 0.5
  textFormat_circular = Ø%(value)3.3f
  textRenderer_color = rgb(0,0,255)
  textRenderer_family = inherit
  textRenderer_size = 3.6
  unit_custom_scale = 1
  unit_scheme = 0
FEATURE [Drawing::FeaturePage] Page001
  EditableTexts = Designed by Name | Date | Scale | Weight | Title | Subtitle | Drawing number | Sheet
  Group = -> [Ortho001,Ortho002,dim001,dim002,centerLines001,centerLines002,centerLines003,dim003,centerLines004,dimStack001,dimStack002,dimStack003,centerLines005,centerLines006,dim004,centerLines007,centerLines008,dim005,dim006,dim007,dim008,dim009,dim010,dia]
  Template = <path>
FEATURE [Part::MultiFuse] Fusion007
  Shapes = -> [Fusion006,Chamfer004,Chamfer005,Chamfer006,Chamfer007]
FEATURE [Part::Fillet] Fillet
  Base = -> Fusion007
  Edges = 10 edges r=3: [Edge58,Edge60,Edge85,Edge100,Edge114,Edge118,Edge134,Edge148,Edge173,Edge183]
FEATURE [Part::Fillet] Fillet001
  Base = -> Cut006
  Edges = 4 edges r=3: [Edge1,Edge3,Edge13,Edge23]
note: 1 file-system path scrubbed to <path> (originals preserved in the JSON sidecar)
